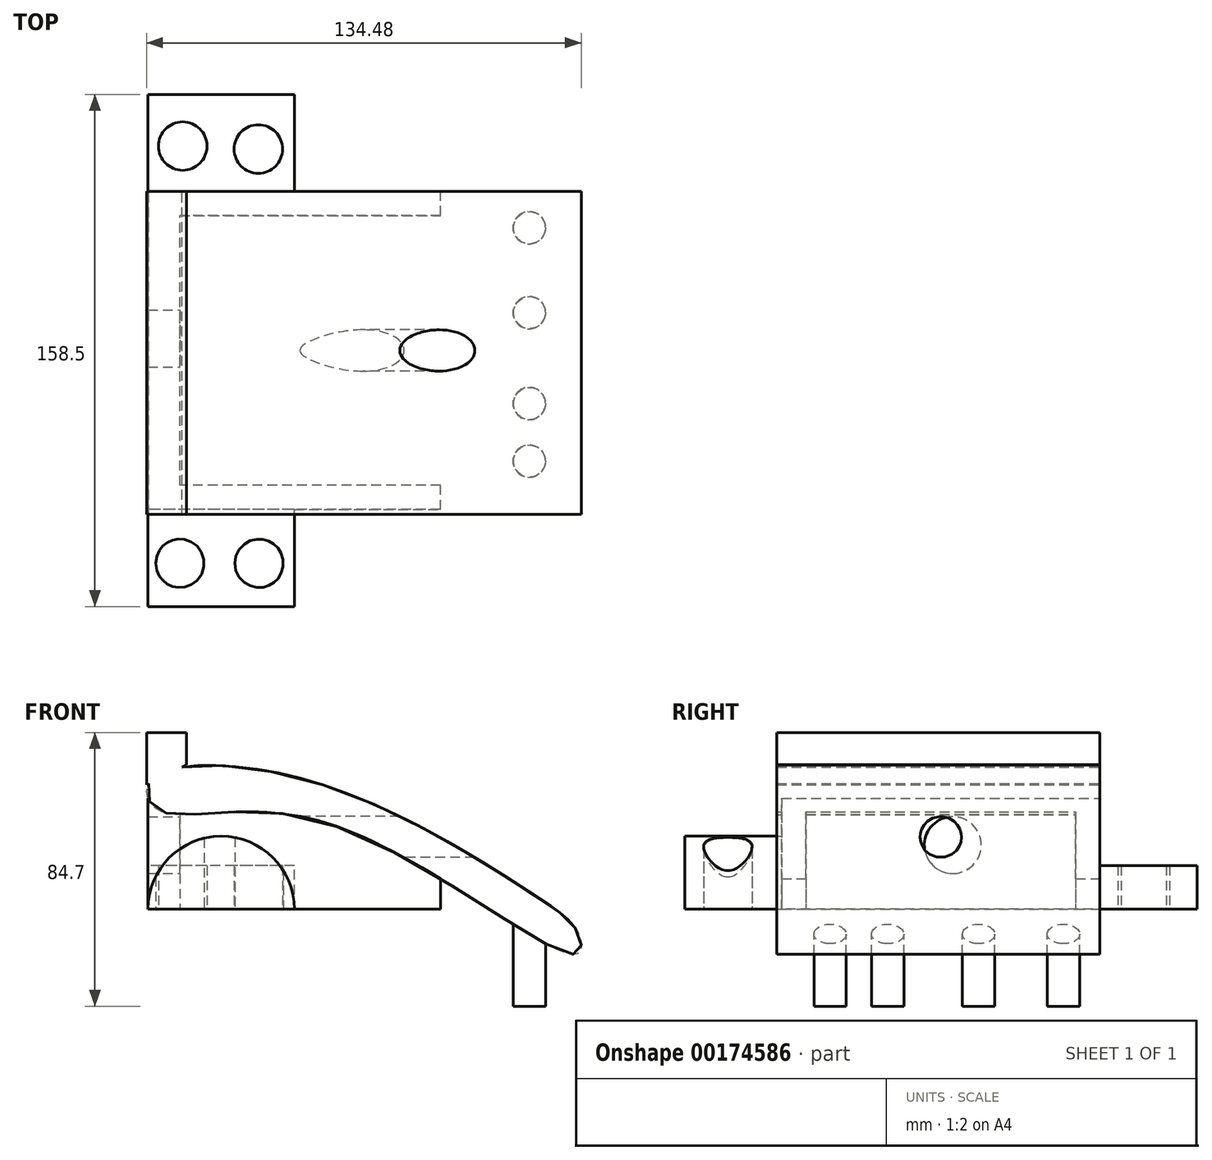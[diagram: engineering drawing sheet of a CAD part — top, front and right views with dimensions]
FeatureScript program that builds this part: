
annotation { "Feature Type Name" : "Feature", "Feature Type Description" : "" }
export const myFeature = defineFeature(function(context is Context, id is Id, definition is map)
    precondition{}
    {
        {
            var Q0;
            Q0=qCreatedBy(makeId("Front.planeOp"),FACE);
            var sketch = newSketch(context, id + "F0", { "sketchPlane" : qUnion([Q0])});
            skFitSpline(sketch, "E0", {"points": [v(-64.53, 39.77) * mm, v(-15.33, 39.77) * mm, v(53.35, 4.95) * mm, v(68.05, -7.83) * mm, v(67.09, -13.9) * mm, v(-12.14, 27.31) * mm, v(-62.3, 30.83) * mm, v(-64.53, 39.77) * mm]});
            skSolve(sketch);
        }
        {
            var Q0;
            Q0=makeQuery(id+"F0.imprint","IMPRINT",FACE,{"disambiguationData":[TD([[makeQuery(id+"F0.imprint","IMPRINT",EDGE,{"derivedFrom":sQuery(id+"F0.wireOp",EDGE,"E0")}),-1.0]])]});
            extrude(context, id + "F1", {"entities" : qUnion([Q0]), "depth" : 100 * mm});
        }
        {
            var Q0;
            Q0=qCreatedBy(makeId("Top.planeOp"),FACE);
            var sketch = newSketch(context, id + "F2", { "sketchPlane" : qUnion([Q0])});
            skCircle(sketch, "E1", {"center": v(52.71, -65.7) * mm, "radius": 5 * mm});
            skCircle(sketch, "E2", {"center": v(52.71, -37.55) * mm, "radius": 5 * mm});
            skCircle(sketch, "E3", {"center": v(52.71, -11.3) * mm, "radius": 5 * mm});
            skCircle(sketch, "E4", {"center": v(52.71, -83.5) * mm, "radius": 5 * mm});
            skSolve(sketch);
        }
        {
            var Q0;
            Q0 = qSketchRegion(id + "F2", true);
            extrude(context, id + "F3", {"entities" : qUnion([Q0]), "operationType" : NewBodyOperationType.ADD, "oppositeDirection" : true, "depth" : 30 * mm});
        }
        {
            var Q0;
            Q0=qCreatedBy(makeId("Top.planeOp"),FACE);
            var sketch = newSketch(context, id + "F4", { "sketchPlane" : qUnion([Q0])});
            skLineSegment(sketch, "E5", {"start": v(25.25, 0) * mm, "end": v(-65.25, 0) * mm});
            skLineSegment(sketch, "E6", {"start": v(-65.25, 0) * mm, "end": v(-65.25, -98.5) * mm});
            skLineSegment(sketch, "E7", {"start": v(-65.25, -98.5) * mm, "end": v(25.25, -98.5) * mm});
            skLineSegment(sketch, "E8", {"start": v(25.25, -98.5) * mm, "end": v(25.25, -91) * mm});
            skLineSegment(sketch, "E9", {"start": v(25.25, -91) * mm, "end": v(-55.4, -91) * mm});
            skLineSegment(sketch, "E10", {"start": v(-55.4, -91) * mm, "end": v(-55.4, -7.5) * mm});
            skLineSegment(sketch, "E11", {"start": v(-55.4, -7.5) * mm, "end": v(25.25, -7.5) * mm});
            skLineSegment(sketch, "E12", {"start": v(25.25, -7.5) * mm, "end": v(25.25, 0) * mm});
            skSolve(sketch);
        }
        {
            var Q0;
            Q0=makeQuery(id+"F4.imprint","IMPRINT",FACE,{"disambiguationData":[TD([[makeQuery(id+"F4.imprint","IMPRINT",EDGE,{"derivedFrom":sQuery(id+"F4.wireOp",EDGE,"E5")}),1.0]])]});
            extrude(context, id + "F5", {"entities" : qUnion([Q0]), "operationType" : NewBodyOperationType.ADD, "endBound" : BoundingType.UP_TO_NEXT, "depth" : 25 * mm});
        }
        {
            var Q0;
            Q0=qCreatedBy(makeId("Front.planeOp"),FACE);
            var sketch = newSketch(context, id + "F6", { "sketchPlane" : qUnion([Q0])});
            skLineSegment(sketch, "E13", {"start": v(-65.7, 38.57) * mm, "end": v(-65.7, 54.7) * mm});
            skLineSegment(sketch, "E14", {"start": v(-65.7, 54.7) * mm, "end": v(-53.38, 54.7) * mm});
            skLineSegment(sketch, "E15", {"start": v(-53.38, 54.7) * mm, "end": v(-53.38, 44.73) * mm});
            skLineSegment(sketch, "E16", {"start": v(-65.7, 38.57) * mm, "end": v(-53.38, 44.73) * mm});
            skSolve(sketch);
        }
        {
            var Q0;
            Q0=makeQuery(id+"F6.imprint","IMPRINT",FACE,{"disambiguationData":[TD([[makeQuery(id+"F6.imprint","IMPRINT",EDGE,{"derivedFrom":sQuery(id+"F6.wireOp",EDGE,"E13")}),-1.0]])]});
            extrude(context, id + "F7", {"entities" : qUnion([Q0]), "operationType" : NewBodyOperationType.ADD, "depth" : 100 * mm});
        }
        {
            var Q0;
            Q0=makeQuery(id+"F5.opExtrude","SWEPT_FACE",FACE,{"disambiguationData":[OSD([sQuery(id+"F4.wireOp",EDGE,"E10")])]});
            var sketch = newSketch(context, id + "F8", { "sketchPlane" : qUnion([Q0])});
            skCircle(sketch, "E17", {"center": v(-49.25, 22.37) * mm, "radius": 6.38 * mm});
            skPoint(sketch, "E17.centerSnap0", {"position": v(-49.25, 0) * mm});
            skSolve(sketch);
        }
        {
            var Q0;
            Q0=makeQuery(id+"F8.imprint","IMPRINT",FACE,{"disambiguationData":[TD([[makeQuery(id+"F8.imprint","IMPRINT",EDGE,{"derivedFrom":sQuery(id+"F8.wireOp",EDGE,"E17")}),1.0]])]});
            extrude(context, id + "F9", {"entities" : qUnion([Q0]), "operationType" : NewBodyOperationType.REMOVE, "endBound" : BoundingType.THROUGH_ALL, "depth" : 25 * mm});
        }
        {
            var Q0;
            Q0=makeQuery(id+"F5.opExtrude","SWEPT_FACE",FACE,{"disambiguationData":[OSD([sQuery(id+"F4.wireOp",EDGE,"E10")])]});
            var sketch = newSketch(context, id + "F10", { "sketchPlane" : qUnion([Q0])});
            skCircle(sketch, "E18", {"center": v(-45.56, 19.86) * mm, "radius": 8.8 * mm});
            skSolve(sketch);
        }
        {
            var Q0;
            Q0=makeQuery(id+"F10.imprint","IMPRINT",FACE,{"disambiguationData":[TD([[makeQuery(id+"F10.imprint","IMPRINT",EDGE,{"derivedFrom":sQuery(id+"F10.wireOp",EDGE,"E18")}),1.0]])]});
            extrude(context, id + "F11", {"entities" : qUnion([Q0]), "operationType" : NewBodyOperationType.REMOVE, "endBound" : BoundingType.THROUGH_ALL, "oppositeDirection" : true, "depth" : 25 * mm});
        }
        {
            var Q0;
            Q0=makeQuery(id+"F7.boolean.opBoolean","MERGE",FACE,{"derivedFrom":[makeQuery(id+"F5.boolean.opBoolean","MERGE",FACE,{"derivedFrom":[makeQuery(id+"F1.opExtrude","CAP_FACE",FACE,{"disambiguationData":[OSD([sQuery(id+"F0.wireOp",EDGE,"E0")])],"isStart":true}),makeQuery(id+"F5.opExtrude","SWEPT_FACE",FACE,{"disambiguationData":[OSD([sQuery(id+"F4.wireOp",EDGE,"E5")])]})]}),makeQuery(id+"F7.opExtrude","CAP_FACE",FACE,{"disambiguationData":[OSD([sQuery(id+"F6.wireOp",EDGE,"E13"),sQuery(id+"F6.wireOp",EDGE,"E14"),sQuery(id+"F6.wireOp",EDGE,"E15"),sQuery(id+"F6.wireOp",EDGE,"E16")])],"isStart":true})]});
            var sketch = newSketch(context, id + "F12", { "sketchPlane" : qUnion([Q0])});
            skLineSegment(sketch, "E19", {"start": v(65.25, 0) * mm, "end": v(20, 0) * mm});
            skLineSegment(sketch, "E20", {"start": v(20, 0) * mm, "end": v(20, 13.47) * mm});
            skLineSegment(sketch, "E21", {"start": v(20, 13.47) * mm, "end": v(65.25, 13.47) * mm});
            skLineSegment(sketch, "E22", {"start": v(65.25, 13.47) * mm, "end": v(65.25, 0) * mm});
            skSolve(sketch);
        }
        {
            var Q0;
            Q0=makeQuery(id+"F12.imprint","IMPRINT",FACE,{"disambiguationData":[TD([[makeQuery(id+"F12.imprint","IMPRINT",EDGE,{"derivedFrom":sQuery(id+"F12.wireOp",EDGE,"E19")}),1.0]])]});
            extrude(context, id + "F13", {"entities" : qUnion([Q0]), "operationType" : NewBodyOperationType.ADD, "depth" : 30 * mm});
        }
        {
            var Q0;
            Q0=makeQuery(id+"F13.boolean.opBoolean","MERGE",FACE,{"derivedFrom":[makeQuery(id+"F5.opExtrude","CAP_FACE",FACE,{"disambiguationData":[OSD([sQuery(id+"F4.wireOp",EDGE,"E5"),sQuery(id+"F4.wireOp",EDGE,"E6"),sQuery(id+"F4.wireOp",EDGE,"E7"),sQuery(id+"F4.wireOp",EDGE,"E8"),sQuery(id+"F4.wireOp",EDGE,"E9"),sQuery(id+"F4.wireOp",EDGE,"E10"),sQuery(id+"F4.wireOp",EDGE,"E11"),sQuery(id+"F4.wireOp",EDGE,"E12")])],"isStart":true}),makeQuery(id+"F13.opExtrude","SWEPT_FACE",FACE,{"disambiguationData":[OSD([sQuery(id+"F12.wireOp",EDGE,"E19")])]})]});
            var sketch = newSketch(context, id + "F14", { "sketchPlane" : qUnion([Q0])});
            skCircle(sketch, "E23", {"center": v(-54.52, -14) * mm, "radius": 7.5 * mm});
            skCircle(sketch, "E24", {"center": v(-31.13, -13.07) * mm, "radius": 7.5 * mm});
            skSolve(sketch);
        }
        {
            var Q0;
            Q0=makeQuery(id+"F14.imprint","IMPRINT",FACE,{"disambiguationData":[TD([[makeQuery(id+"F14.imprint","IMPRINT",EDGE,{"derivedFrom":sQuery(id+"F14.wireOp",EDGE,"E23")}),1.0]])]});
            var Q1;
            Q1=makeQuery(id+"F14.imprint","IMPRINT",FACE,{"disambiguationData":[TD([[makeQuery(id+"F14.imprint","IMPRINT",EDGE,{"derivedFrom":sQuery(id+"F14.wireOp",EDGE,"E24")}),1.0]])]});
            extrude(context, id + "F15", {"entities" : qUnion([Q0, Q1]), "operationType" : NewBodyOperationType.REMOVE, "endBound" : BoundingType.THROUGH_ALL, "oppositeDirection" : true, "depth" : 25 * mm});
        }
        {
            var Q0;
            Q0=makeQuery(id+"F5.opExtrude","SWEPT_FACE",FACE,{"disambiguationData":[OSD([sQuery(id+"F4.wireOp",EDGE,"E7")])]});
            var sketch = newSketch(context, id + "F16", { "sketchPlane" : qUnion([Q0])});
            skArc(sketch, "E25", {"start": v(-20, 0) * mm, "mid": v(-42.63, 22.63) * mm, "end": v(-65.25, 0) * mm});
            skLineSegment(sketch, "E26", {"start": v(-65.25, 0) * mm, "end": v(-20, 0) * mm});
            skSolve(sketch);
        }
        {
            var Q0;
            Q0=makeQuery(id+"F16.imprint","IMPRINT",FACE,{"disambiguationData":[TD([[makeQuery(id+"F16.imprint","IMPRINT",EDGE,{"derivedFrom":sQuery(id+"F16.wireOp",EDGE,"E25")}),1.0]])]});
            extrude(context, id + "F17", {"entities" : qUnion([Q0]), "operationType" : NewBodyOperationType.ADD, "depth" : 30 * mm});
        }
        {
            var Q0;
            Q0=makeQuery(id+"F17.boolean.opBoolean","MERGE",FACE,{"derivedFrom":[makeQuery(id+"F13.boolean.opBoolean","MERGE",FACE,{"derivedFrom":[makeQuery(id+"F5.opExtrude","CAP_FACE",FACE,{"disambiguationData":[OSD([sQuery(id+"F4.wireOp",EDGE,"E5"),sQuery(id+"F4.wireOp",EDGE,"E6"),sQuery(id+"F4.wireOp",EDGE,"E7"),sQuery(id+"F4.wireOp",EDGE,"E8"),sQuery(id+"F4.wireOp",EDGE,"E9"),sQuery(id+"F4.wireOp",EDGE,"E10"),sQuery(id+"F4.wireOp",EDGE,"E11"),sQuery(id+"F4.wireOp",EDGE,"E12")])],"isStart":true}),makeQuery(id+"F13.opExtrude","SWEPT_FACE",FACE,{"disambiguationData":[OSD([sQuery(id+"F12.wireOp",EDGE,"E19")])]})]}),makeQuery(id+"F17.opExtrude","SWEPT_FACE",FACE,{"disambiguationData":[OSD([sQuery(id+"F16.wireOp",EDGE,"E26")])]})]});
            var sketch = newSketch(context, id + "F18", { "sketchPlane" : qUnion([Q0])});
            skCircle(sketch, "E27", {"center": v(-55.4, 115.13) * mm, "radius": 7.5 * mm});
            skCircle(sketch, "E28", {"center": v(-30.9, 115.13) * mm, "radius": 7.5 * mm});
            skSolve(sketch);
        }
        {
            var Q0;
            Q0=makeQuery(id+"F18.imprint","IMPRINT",FACE,{"disambiguationData":[TD([[makeQuery(id+"F18.imprint","IMPRINT",EDGE,{"derivedFrom":sQuery(id+"F18.wireOp",EDGE,"E27")}),1.0]])]});
            var Q1;
            Q1=makeQuery(id+"F18.imprint","IMPRINT",FACE,{"disambiguationData":[TD([[makeQuery(id+"F18.imprint","IMPRINT",EDGE,{"derivedFrom":sQuery(id+"F18.wireOp",EDGE,"E28")}),1.0]])]});
            extrude(context, id + "F19", {"entities" : qUnion([Q0, Q1]), "operationType" : NewBodyOperationType.REMOVE, "endBound" : BoundingType.THROUGH_ALL, "oppositeDirection" : true, "depth" : 25 * mm});
        }
    });
